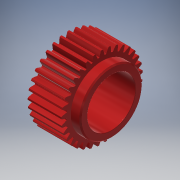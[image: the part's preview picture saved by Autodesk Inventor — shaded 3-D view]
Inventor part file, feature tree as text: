
AUTODESK INVENTOR PART (.ipt)
format: ipt  version: 2018 (Build 220112000, 112)  size: 610,816 bytes
history: native  units: mm
features: extrude x2, sketch x1, fillet x1, chamfer x1
ambient origin geometry x8: Origin, YZ Plane, XZ Plane, XY Plane, X Axis, Y Axis, Z Axis, Center Point
bodies: Solid1 (feature_tree)
feature tree (5):
  sketch  "Sketch1"  dims[d0=10.0mm d1=16.98mm d2=14.74mm d3=13.0mm d4=5.25mm d5=0.2mm d6=0.13mm d7=0.61mm d8=330.0mm d10=360.0deg d12=7.0mm d13=0.0mm d14=2.0mm d15=0.0mm d16=0.1mm d17=0.25mm d18=2.0mm d19=45.0deg]
  extrude  "Extrusion1"  Depth=2.0mm
  extrude  "Extrusion2"  Depth=2.0mm
  fillet  "Fillet1"  Radius=5.25mm
  chamfer  "Chamfer1"  Distance=0.2mm
